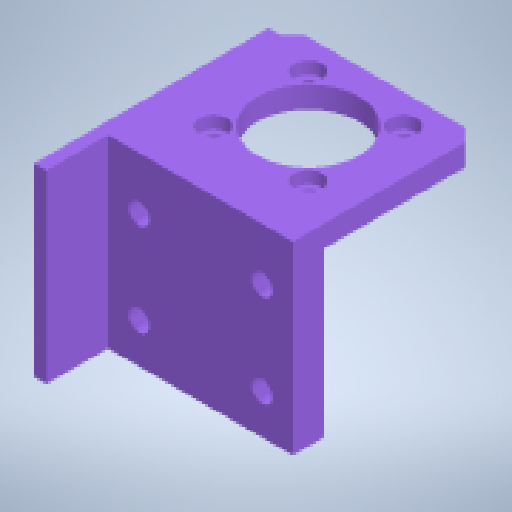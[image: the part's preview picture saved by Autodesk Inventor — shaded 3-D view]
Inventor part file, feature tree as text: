
AUTODESK INVENTOR PART (.ipt)
format: ipt  version: 2025.1 (Build 291241000, 241)  size: 313,344 bytes
history: native  units: mm
features: sketch x5, extrude x3, hole x2
ambient origin geometry x8: Origin, YZ Plane, XZ Plane, XY Plane, X Axis, Y Axis, Z Axis, Center Point
bodies: Solide1 (feature_tree)
feature tree (10):
  extrude  "Extrusion1"  Depth=25.0mm
  hole  "Perçage1"  [1 undecoded]
  extrude  "Extrusion2"  Depth=16.5mm
  extrude  "Extrusion3"  Depth=15.0mm
  hole  "Perçage2"  [1 undecoded]
  sketch  "Esquisse1"
  sketch  "Esquisse2"
  sketch  "Esquisse3"
  sketch  "Esquisse4"
  sketch  "Esquisse5"
note: 2 required parameter values undecoded (feature->parameter linkage not recoverable at this tier; creation-order binding heuristic only, values carry confidence <= 0.55)
